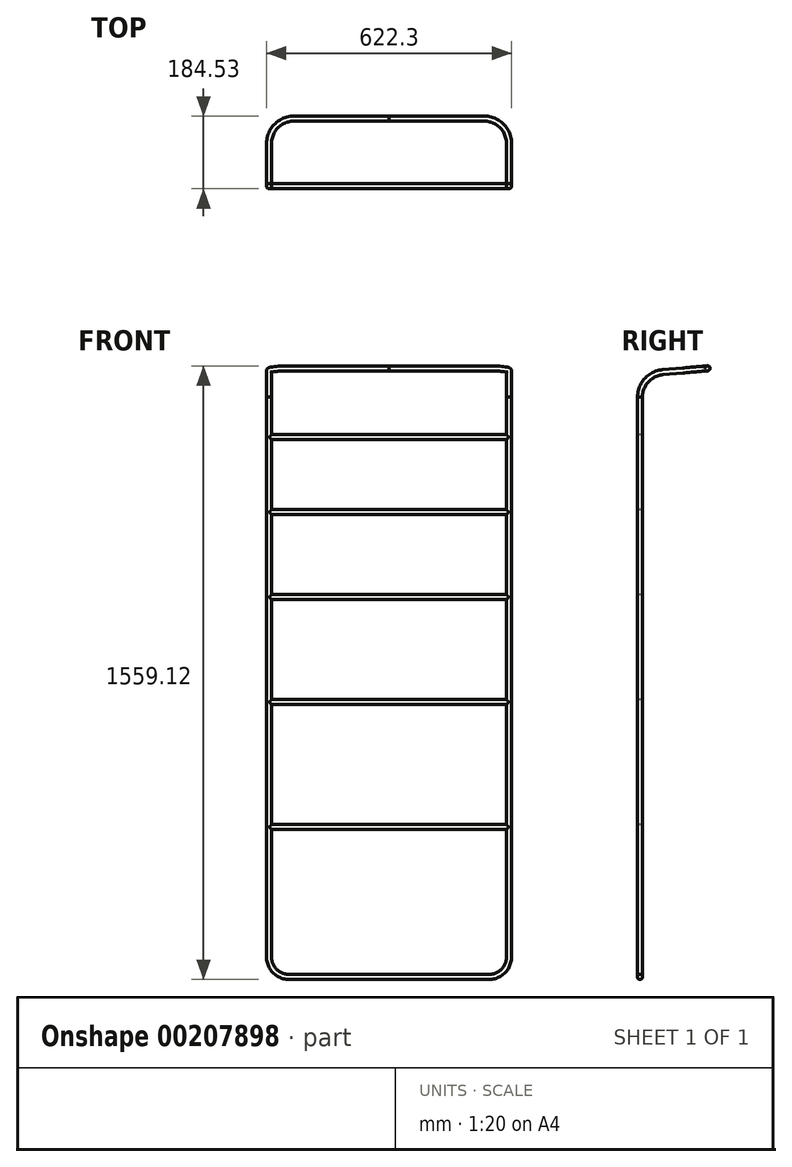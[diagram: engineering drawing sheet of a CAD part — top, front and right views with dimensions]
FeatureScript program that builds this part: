
annotation { "Feature Type Name" : "Feature", "Feature Type Description" : "" }
export const myFeature = defineFeature(function(context is Context, id is Id, definition is map)
    precondition{}
    {
        {
            var Q0;
            Q0=qCreatedBy(makeId("Front.planeOp"),FACE);
            var sketch = newSketch(context, id + "F0", { "sketchPlane" : qUnion([Q0])});
            skLineSegment(sketch, "E0.bottom", {"start": v(-254, 762) * mm, "end": v(254, 762) * mm});
            skLineSegment(sketch, "E0.left", {"start": v(-304.8, 711.2) * mm, "end": v(-304.8, 0) * mm});
            skLineSegment(sketch, "E0.right", {"start": v(304.8, 711.2) * mm, "end": v(304.8, 0) * mm});
            skLineSegment(sketch, "E1", {"start": v(0, 762) * mm, "end": v(0, -762) * mm, "construction": true});
            skLineSegment(sketch, "E2", {"start": v(-304.8, 0) * mm, "end": v(304.8, 0) * mm, "construction": true});
            skPoint(sketch, "E3.visualSharp", {"position": v(-304.8, 762) * mm});
            skArc(sketch, "E3.filletArc", {"start": v(-254, 762) * mm, "mid": v(-289.92, 747.12) * mm, "end": v(-304.8, 711.2) * mm});
            skPoint(sketch, "E4.visualSharp", {"position": v(304.8, 762) * mm});
            skArc(sketch, "E4.filletArc", {"start": v(304.8, 711.2) * mm, "mid": v(289.92, 747.12) * mm, "end": v(254, 762) * mm});
            skLineSegment(sketch, "E5.MirrorCS", {"start": v(-304.8, -711.2) * mm, "end": v(-304.8, 0) * mm});
            skArc(sketch, "E6.MirrorCS", {"start": v(-254, -762) * mm, "mid": v(-289.92, -747.12) * mm, "end": v(-304.8, -711.2) * mm});
            skLineSegment(sketch, "E7.MirrorCS", {"start": v(-254, -762) * mm, "end": v(254, -762) * mm});
            skPoint(sketch, "E8.MirrorP", {"position": v(304.8, -762) * mm});
            skArc(sketch, "E9.MirrorCS", {"start": v(304.8, -711.2) * mm, "mid": v(289.92, -747.12) * mm, "end": v(254, -762) * mm});
            skLineSegment(sketch, "E10.MirrorCS", {"start": v(304.8, -711.2) * mm, "end": v(304.8, 0) * mm});
            skSolve(sketch);
        }
        {
            var Q0;
            Q0=qCreatedBy(makeId("Top.planeOp"),FACE);
            var sketch = newSketch(context, id + "F1", { "sketchPlane" : qUnion([Q0])});
            skCircle(sketch, "E11", {"center": v(304.8, 0) * mm, "radius": 6.35 * mm});
            skSolve(sketch);
        }
        {
            var Q0;
            Q0=makeQuery(id+"F1.imprint","IMPRINT",FACE,{"disambiguationData":[TD([[makeQuery(id+"F1.imprint","IMPRINT",EDGE,{"derivedFrom":sQuery(id+"F1.wireOp",EDGE,"E11")}),1.0]])]});
            var Q1;
            Q1=sQuery(id+"F0.wireOp",EDGE,"E0.right");
            var Q2;
            Q2=sQuery(id+"F0.wireOp",EDGE,"E4.filletArc");
            var Q3;
            Q3=sQuery(id+"F0.wireOp",EDGE,"E0.bottom");
            var Q4;
            Q4=sQuery(id+"F0.wireOp",EDGE,"E3.filletArc");
            var Q5;
            Q5=sQuery(id+"F0.wireOp",EDGE,"E0.left");
            sweep(context, id + "F2", {"profiles" : qUnion([Q0]), "path" : qUnion([Q1, Q2, Q3, Q4, Q5])});
        }
        {
            var Q0;
            Q0=makeQuery(id+"F2.opSweep","SWEPT_BODY",BODY,{"disambiguationData":[OSD([sQuery(id+"F0.wireOp",EDGE,"E0.left"),sQuery(id+"F1.wireOp",EDGE,"E11")])]});
            var Q1;
            Q1=qCreatedBy(makeId("Top.planeOp"),FACE);
            mirror(context, id + "F3", {"operationType" : NewBodyOperationType.ADD, "entities" : qUnion([Q0]), "mirrorPlane" : qUnion([Q1])});
        }
        {
            var Q0;
            Q0=qCreatedBy(makeId("Front.planeOp"),FACE);
            var sketch = newSketch(context, id + "F4", { "sketchPlane" : qUnion([Q0])});
            skLineSegment(sketch, "E12", {"start": v(-304.8, 609.6) * mm, "end": v(304.8, 609.6) * mm});
            skLineSegment(sketch, "E13", {"start": v(-304.8, 419.1) * mm, "end": v(304.8, 419.1) * mm});
            skLineSegment(sketch, "E14", {"start": v(-304.8, 203.2) * mm, "end": v(304.8, 203.2) * mm});
            skLineSegment(sketch, "E15", {"start": v(-304.8, -63.5) * mm, "end": v(304.8, -63.5) * mm});
            skLineSegment(sketch, "E16", {"start": v(-304.8, -381) * mm, "end": v(304.8, -381) * mm});
            skSolve(sketch);
        }
        {
            var Q0;
            Q0=qCreatedBy(makeId("Right.planeOp"),FACE);
            var sketch = newSketch(context, id + "F5", { "sketchPlane" : qUnion([Q0])});
            skCircle(sketch, "E17", {"center": v(0, -381) * mm, "radius": 6.35 * mm});
            skCircle(sketch, "E18", {"center": v(0, -63.5) * mm, "radius": 6.35 * mm});
            skCircle(sketch, "E19", {"center": v(0, 203.2) * mm, "radius": 6.35 * mm});
            skCircle(sketch, "E20", {"center": v(0, 419.1) * mm, "radius": 6.35 * mm});
            skCircle(sketch, "E21", {"center": v(0, 609.6) * mm, "radius": 6.35 * mm});
            skSolve(sketch);
        }
        {
            var Q0;
            Q0 = qSketchRegion(id + "F5", true);
            extrude(context, id + "F6", {"entities" : qUnion([Q0]), "operationType" : NewBodyOperationType.ADD, "endBound" : BoundingType.SYMMETRIC, "depth" : 609.6 * mm});
        }
        {
            var Q0;
            Q0=qCreatedBy(makeId("Right.planeOp"),FACE);
            var Q1;
            Q1=sQuery(id+"F0.wireOp",VERTEX,"E0.right.start");
            cPlane(context, id + "F7", {"entities" : qUnion([Q0, Q1]), "cplaneType" : CPlaneType.PLANE_POINT, "offset" : 25.4 * mm, "width" : 152.4 * mm, "height" : 152.4 * mm});
        }
        {
            var Q0;
            Q0=qCreatedBy(makeId("Front.planeOp"),FACE);
            var sketch = newSketch(context, id + "F8", { "sketchPlane" : qUnion([Q0])});
            skLineSegment(sketch, "E22.bottom", {"start": v(-378.75, 711.2) * mm, "end": v(373.61, 711.2) * mm});
            skLineSegment(sketch, "E22.top", {"start": v(-378.75, 843.4) * mm, "end": v(373.61, 843.4) * mm});
            skLineSegment(sketch, "E22.left", {"start": v(-378.75, 711.2) * mm, "end": v(-378.75, 843.4) * mm});
            skLineSegment(sketch, "E22.right", {"start": v(373.61, 711.2) * mm, "end": v(373.61, 843.4) * mm});
            skSolve(sketch);
        }
        {
            var Q0;
            Q0 = qSketchRegion(id + "F8", true);
            extrude(context, id + "F9", {"entities" : qUnion([Q0]), "operationType" : NewBodyOperationType.REMOVE, "endBound" : BoundingType.SYMMETRIC, "oppositeDirection" : true, "depth" : 137.16 * mm, "offsetDistance" : 25.4 * mm});
        }
        {
            var Q0;
            Q0=qCreatedBy(id+"F7.planeOp",FACE);
            var sketch = newSketch(context, id + "F10", { "sketchPlane" : qUnion([Q0])});
            skArc(sketch, "E23", {"start": v(57.97, 774.46) * mm, "mid": v(16.68, 754.1) * mm, "end": v(0, 711.2) * mm});
            skLineSegment(sketch, "E24", {"start": v(0, 711.2) * mm, "end": v(63.5, 711.2) * mm, "construction": true});
            skLineSegment(sketch, "E25", {"start": v(63.5, 711.2) * mm, "end": v(57.97, 774.46) * mm, "construction": true});
            skLineSegment(sketch, "E26", {"start": v(57.97, 774.46) * mm, "end": v(108.57, 778.89) * mm});
            skLineSegment(sketch, "E27", {"start": v(0, 711.2) * mm, "end": v(0, 665.62) * mm, "construction": true});
            skSolve(sketch);
        }
        {
            var Q0;
            Q0=sQuery(id+"F10.wireOp",EDGE,"E26");
            cPlane(context, id + "F11", {"entities" : qUnion([Q0]), "cplaneType" : CPlaneType.LINE_ANGLE, "offset" : 25.4 * mm, "angle" : 0 * degree, "width" : 152.4 * mm, "height" : 152.4 * mm});
        }
        {
            var Q0;
            Q0=qCreatedBy(id+"F11.planeOp",FACE);
            var sketch = newSketch(context, id + "F12", { "sketchPlane" : qUnion([Q0])});
            skArc(sketch, "E28", {"start": v(304.8, 176.04) * mm, "mid": v(286.2, 220.94) * mm, "end": v(241.3, 239.54) * mm});
            skLineSegment(sketch, "E29", {"start": v(241.3, 239.54) * mm, "end": v(0, 239.54) * mm});
            skLineSegment(sketch, "E30", {"start": v(0, 239.54) * mm, "end": v(0, 66.41) * mm, "construction": true});
            skSolve(sketch);
        }
        {
            var Q0;
            {var subQ0=makeQuery(id+"F2.opSweep","SWEPT_FACE",FACE,{"disambiguationData":[OSD([sQuery(id+"F0.wireOp",EDGE,"E0.right"),sQuery(id+"F1.wireOp",EDGE,"E11")])]});Q0=makeQuery(id+"F9.boolean.opBoolean","COPY",FACE,{"disambiguationData":[TD([subQ0])],"derivedFrom":makeQuery(id+"F9.opExtrude","SWEPT_FACE",FACE,{"disambiguationData":[OSD([sQuery(id+"F8.wireOp",EDGE,"E22.bottom")])]})});}
            var sketch = newSketch(context, id + "F13", { "sketchPlane" : qUnion([Q0])});
            skCircle(sketch, "E31.0", {"center": v(304.8, 0) * mm, "radius": 6.35 * mm});
            skSolve(sketch);
        }
        {
            var Q0;
            Q0 = qSketchRegion(id + "F13", true);
            var Q1;
            Q1 = qConstructionFilter(qBodyType(qCreatedBy(id + "F10" ,EDGE), BodyType.WIRE), ConstructionObject.NO);
            sweep(context, id + "F14", {"profiles" : qUnion([Q0]), "path" : qUnion([Q1])});
        }
        {
            var Q0;
            Q0=makeQuery(id+"F14.opSweep","CAP_FACE",FACE,{"disambiguationData":[OSD([sQuery(id+"F10.wireOp",VERTEX,"E26.end"),sQuery(id+"F13.wireOp",EDGE,"E31.0")])],"isStart":false});
            var Q1;
            Q1=sQuery(id+"F12.wireOp",EDGE,"E28");
            var Q2;
            Q2=sQuery(id+"F12.wireOp",EDGE,"E29");
            sweep(context, id + "F15", {"operationType" : NewBodyOperationType.ADD, "profiles" : qUnion([Q0]), "path" : qUnion([Q1, Q2])});
        }
        {
            var Q0;
            Q0=makeQuery(id+"F15.opSweep","SWEPT_BODY",BODY,{"disambiguationData":[OSD([sQuery(id+"F10.wireOp",VERTEX,"E26.end"),sQuery(id+"F12.wireOp",EDGE,"E29"),sQuery(id+"F13.wireOp",EDGE,"E31.0")])]});
            var Q1;
            Q1=makeQuery(id+"F14.opSweep","SWEPT_BODY",BODY,{"disambiguationData":[OSD([sQuery(id+"F10.wireOp",EDGE,"E26"),sQuery(id+"F13.wireOp",EDGE,"E31.0")])]});
            var Q2;
            Q2=qCreatedBy(makeId("Right.planeOp"),FACE);
            mirror(context, id + "F16", {"entities" : qUnion([Q0, Q1]), "mirrorPlane" : qUnion([Q2])});
        }
    });
